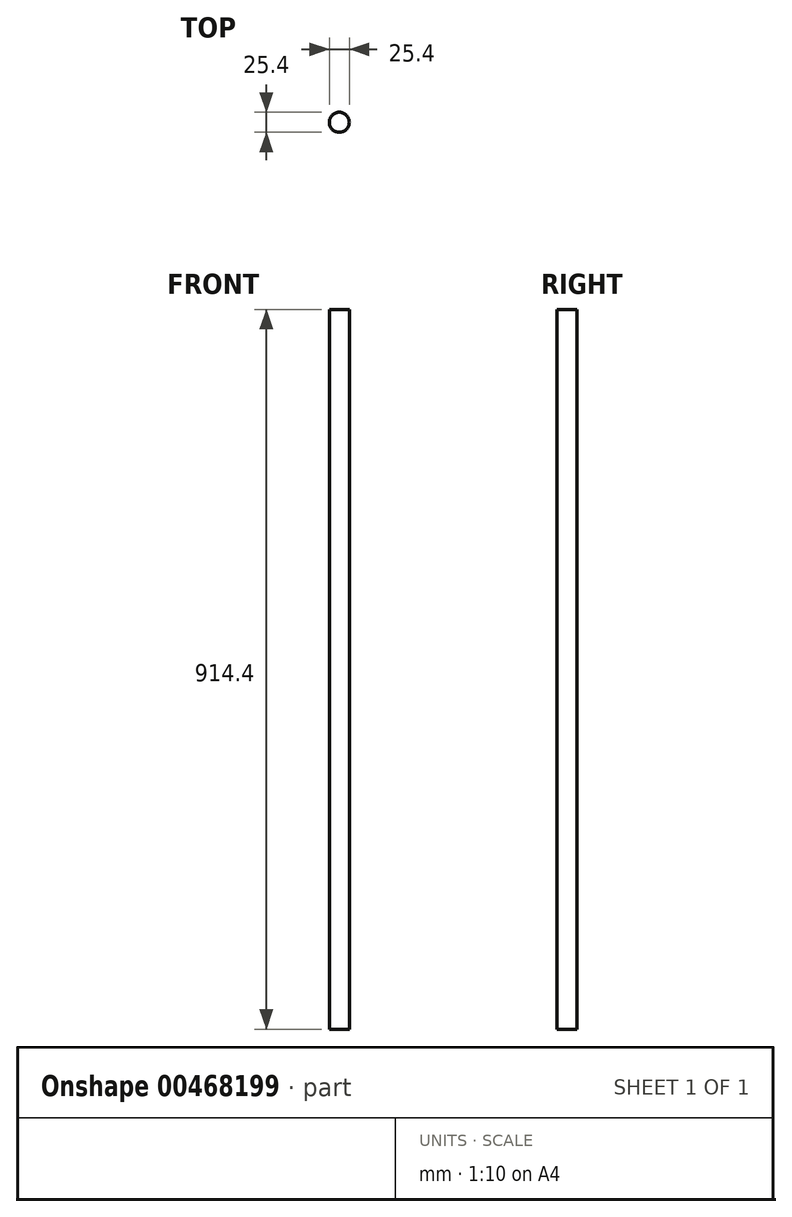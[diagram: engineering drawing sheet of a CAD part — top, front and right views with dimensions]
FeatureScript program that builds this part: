
annotation { "Feature Type Name" : "Feature", "Feature Type Description" : "" }
export const myFeature = defineFeature(function(context is Context, id is Id, definition is map)
    precondition{}
    {
        {
            var Q0;
            Q0=qCreatedBy(makeId("Top.planeOp"),FACE);
            var sketch = newSketch(context, id + "F0", { "sketchPlane" : qUnion([Q0])});
            skCircle(sketch, "E0", {"center": v(0, 0) * mm, "radius": 12.7 * mm});
            skSolve(sketch);
        }
        {
            var Q0;
            Q0=makeQuery(id+"F0.imprint","IMPRINT",FACE,{"disambiguationData":[TD([[makeQuery(id+"F0.imprint","IMPRINT",EDGE,{"derivedFrom":sQuery(id+"F0.wireOp",EDGE,"E0")}),1.0]])]});
            extrude(context, id + "F1", {"entities" : qUnion([Q0]), "depth" : 914.4 * mm});
        }
    });
